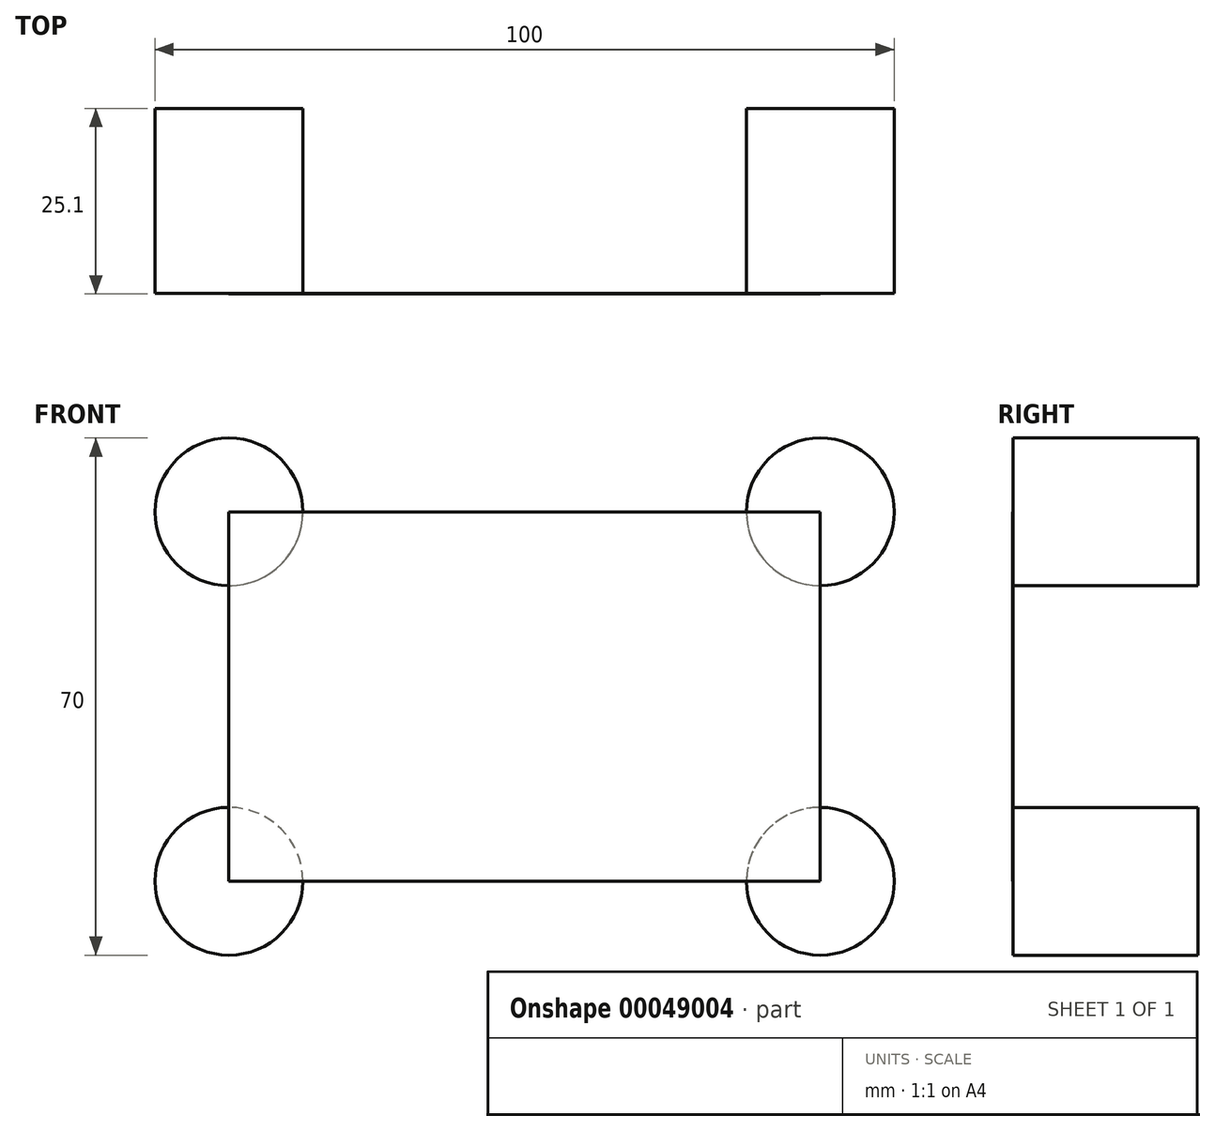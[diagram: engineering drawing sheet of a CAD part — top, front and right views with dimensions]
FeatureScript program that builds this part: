
annotation { "Feature Type Name" : "Feature", "Feature Type Description" : "" }
export const myFeature = defineFeature(function(context is Context, id is Id, definition is map)
    precondition{}
    {
        {
            var Q0;
            Q0=qCreatedBy(makeId("Front.planeOp"),FACE);
            var sketch = newSketch(context, id + "F0", { "sketchPlane" : qUnion([Q0])});
            skCircle(sketch, "E0", {"center": v(-40, -25) * mm, "radius": 10 * mm});
            skCircle(sketch, "E1.0.1.0", {"center": v(-40, 25) * mm, "radius": 10 * mm});
            skCircle(sketch, "E1.1.0.0", {"center": v(40, -25) * mm, "radius": 10 * mm});
            skCircle(sketch, "E1.1.1.0", {"center": v(40, 25) * mm, "radius": 10 * mm});
            skLineSegment(sketch, "E1.direction1", {"start": v(-40, -25) * mm, "end": v(40, -25) * mm, "construction": true});
            skLineSegment(sketch, "E1.direction2", {"start": v(-40, -25) * mm, "end": v(-40, 25) * mm, "construction": true});
            skSolve(sketch);
        }
        {
            var Q0;
            Q0 = qSketchRegion(id + "F0", true);
            extrude(context, id + "F1", {"entities" : qUnion([Q0]), "depth" : 25 * mm});
        }
        {
            var Q0;
            Q0=makeQuery(id+"F1.opExtrude","CAP_FACE",FACE,{"disambiguationData":[OSD([sQuery(id+"F0.wireOp",EDGE,"E1.0.1.0")])],"isStart":false});
            var sketch = newSketch(context, id + "F2", { "sketchPlane" : qUnion([Q0])});
            skLineSegment(sketch, "E2.bottom", {"start": v(-40, 25) * mm, "end": v(40, 25) * mm});
            skLineSegment(sketch, "E2.top", {"start": v(-40, -25) * mm, "end": v(40, -25) * mm});
            skLineSegment(sketch, "E2.left", {"start": v(-40, 25) * mm, "end": v(-40, -25) * mm});
            skLineSegment(sketch, "E2.right", {"start": v(40, 25) * mm, "end": v(40, -25) * mm});
            skSolve(sketch);
        }
        {
            var Q0;
            Q0 = qSketchRegion(id + "F2", true);
            extrude(context, id + "F3", {"entities" : qUnion([Q0]), "depth" : 0.1 * mm});
        }
    });
